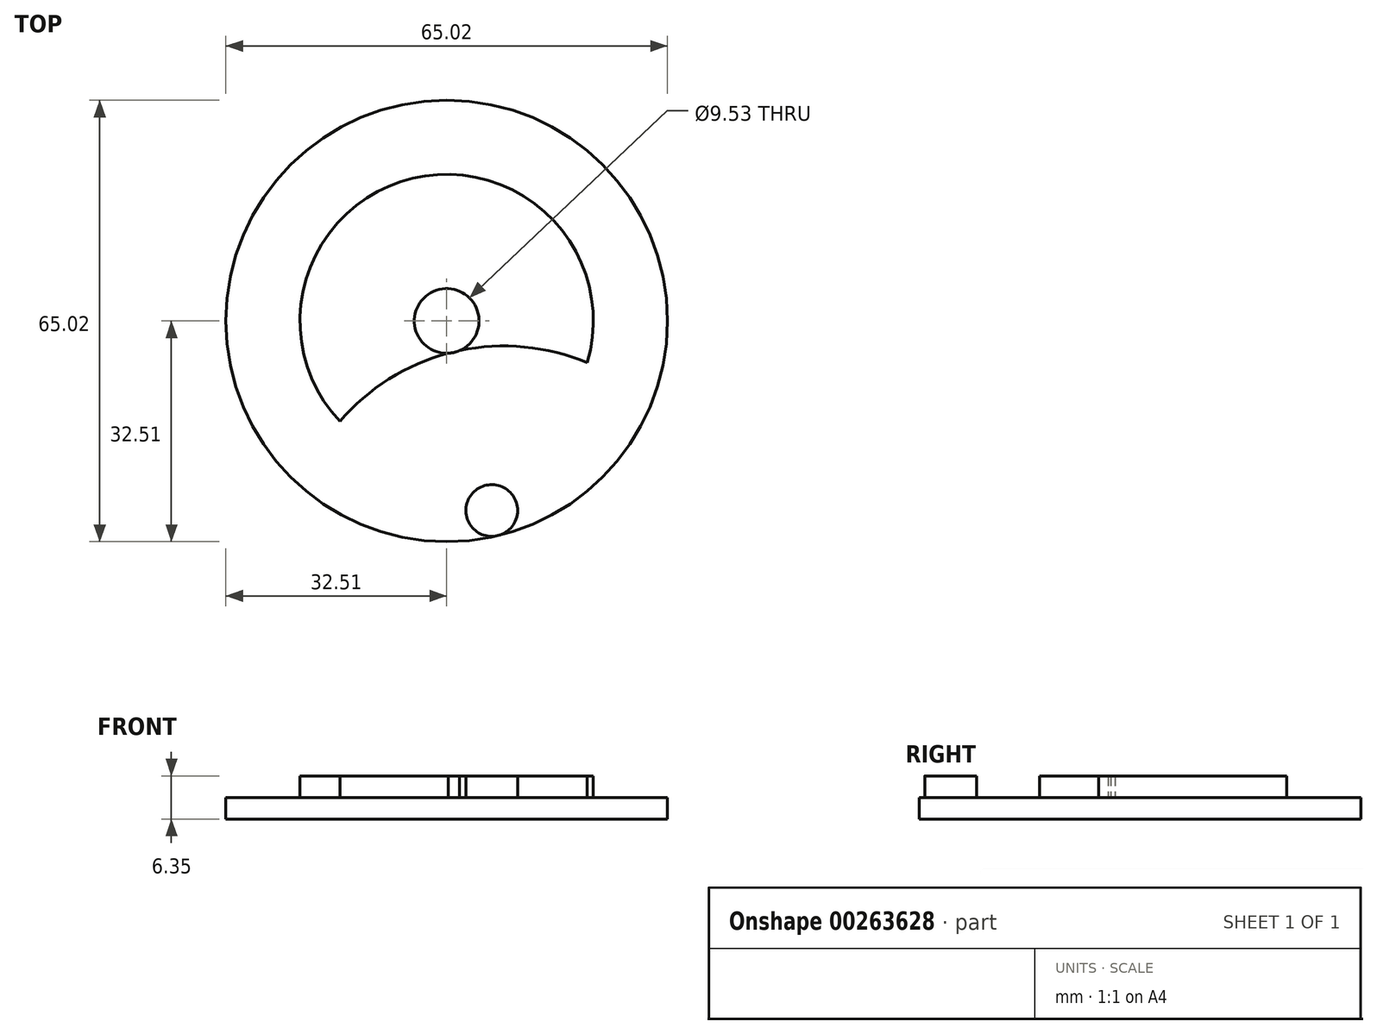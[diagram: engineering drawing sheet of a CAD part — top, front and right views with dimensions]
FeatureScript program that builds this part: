
annotation { "Feature Type Name" : "Feature", "Feature Type Description" : "" }
export const myFeature = defineFeature(function(context is Context, id is Id, definition is map)
    precondition{}
    {
        {
            var Q0;
            Q0=qCreatedBy(makeId("Top.planeOp"),FACE);
            var sketch = newSketch(context, id + "F0", { "sketchPlane" : qUnion([Q0])});
            skCircle(sketch, "E0", {"center": v(0, 0) * mm, "radius": 32.51 * mm});
            skCircle(sketch, "E1", {"center": v(0, 0) * mm, "radius": 4.76 * mm});
            skSolve(sketch);
        }
        {
            var Q0;
            Q0=makeQuery(id+"F0.imprint","IMPRINT",FACE,{"disambiguationData":[TD([[makeQuery(id+"F0.imprint","IMPRINT",EDGE,{"derivedFrom":sQuery(id+"F0.wireOp",EDGE,"E0")}),1.0]])]});
            extrude(context, id + "F1", {"entities" : qUnion([Q0]), "depth" : 3.17 * mm});
        }
        {
            var Q0;
            Q0=makeQuery(id+"F1.opExtrude","CAP_FACE",FACE,{"disambiguationData":[OSD([sQuery(id+"F0.wireOp",EDGE,"E0")])],"isStart":false});
            var sketch = newSketch(context, id + "F2", { "sketchPlane" : qUnion([Q0])});
            skArc(sketch, "E2", {"start": v(20.7, -6.16) * mm, "mid": v(-4.99, 21) * mm, "end": v(-15.71, -14.8) * mm});
            skArc(sketch, "E3", {"start": v(20.7, -6.16) * mm, "mid": v(1.08, -4.55) * mm, "end": v(-15.71, -14.8) * mm});
            skCircle(sketch, "E4", {"center": v(6.63, -27.93) * mm, "radius": 3.81 * mm});
            skCircle(sketch, "E5", {"center": v(0, 0) * mm, "radius": 4.76 * mm});
            skSolve(sketch);
        }
        {
            var Q0;
            Q0=makeQuery(id+"F2.imprint","IMPRINT",FACE,{"disambiguationData":[TD([[makeQuery(id+"F2.imprint","IMPRINT",EDGE,{"derivedFrom":sQuery(id+"F2.wireOp",EDGE,"E2")}),1.0]])]});
            var Q1;
            Q1=makeQuery(id+"F2.imprint","IMPRINT",FACE,{"disambiguationData":[TD([[makeQuery(id+"F2.imprint","IMPRINT",EDGE,{"derivedFrom":sQuery(id+"F2.wireOp",EDGE,"E4")}),1.0]])]});
            extrude(context, id + "F3", {"entities" : qUnion([Q0, Q1]), "operationType" : NewBodyOperationType.ADD, "depth" : 3.17 * mm});
        }
    });
